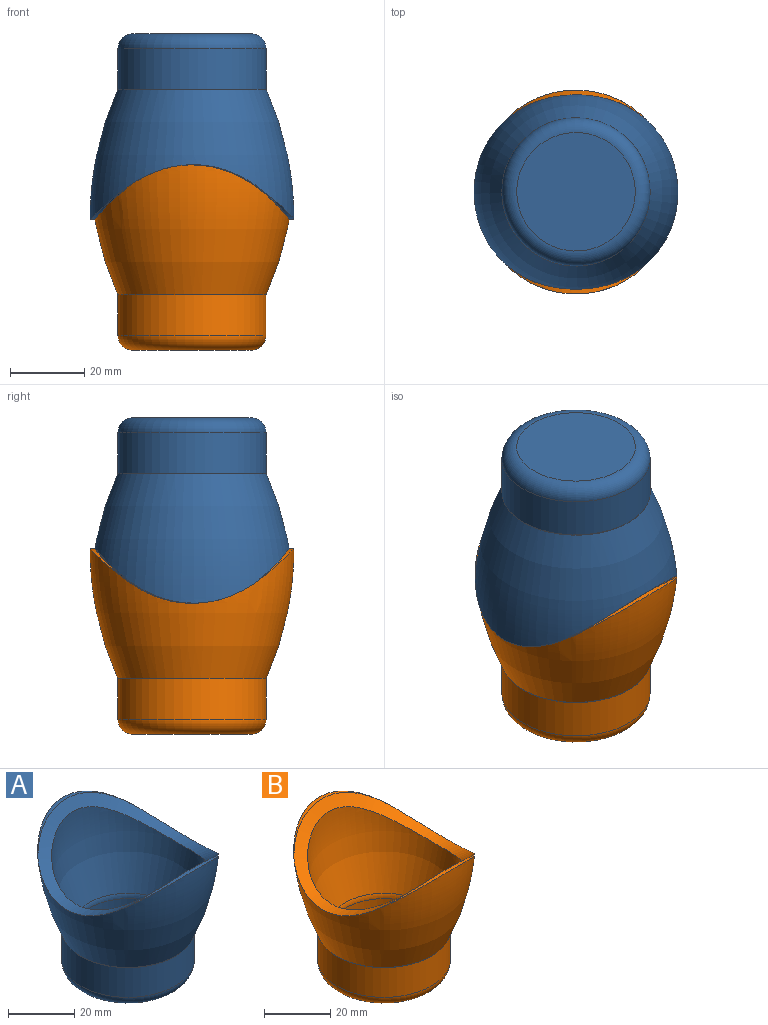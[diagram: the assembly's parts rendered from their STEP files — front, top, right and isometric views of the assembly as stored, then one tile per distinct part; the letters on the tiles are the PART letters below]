
ASSEMBLY  parts=2 mates=1
PART A: 12 faces, bbox 54.9x55x50 mm
  f0: revolved ~54.94x54.94mm, area 4386.3mm2, adj f1,f2,f6,f7
  f1: extruded ~40.09x9.24mm, area 34.4mm2, adj f0,f7
  f2: extruded ~40.09x9.24mm, area 34.3mm2, adj f0,f7
  f3: plane 32x32mm, normal (0,0,-1), area 804.2mm2, adj f5
  f4: cylinder r=20mm len=40mm, axis (0,0,-1), area 1376.9mm2, adj f5,f6
  f5: torus R=16mm, axis (0,0,-1), area 732.2mm2, adj f3,f4
  f6: torus R=20.2mm, axis (0,0,-1), area 10.6mm2, adj f0,f4
  f7: extruded ~52.46x52.45mm, area 724.9mm2, adj f0,f1,f2,f11
  f8: plane 32x32mm, normal (0,0,1), area 804.2mm2, adj f9
  f9: cylinder r=16mm len=32mm, axis (0,0,-1), area 1101.5mm2, adj f8,f10
  f10: torus R=20.2mm, axis (0,0,-1), area 179.4mm2, adj f9,f11
  f11: revolved ~46.86x46.86mm, area 3196.2mm2, adj f7,f10
PART B: 12 faces, bbox 54.9x55x50 mm
  f0: revolved ~54.94x54.94mm, area 4386.3mm2, adj f1,f2,f6,f7
  f1: extruded ~40.09x9.24mm, area 34.4mm2, adj f0,f7
  f2: extruded ~40.09x9.24mm, area 34.3mm2, adj f0,f7
  f3: plane 32x32mm, normal (0,0,-1), area 804.2mm2, adj f5
  f4: cylinder r=20mm len=40mm, axis (0,0,-1), area 1376.9mm2, adj f5,f6
  f5: torus R=16mm, axis (0,0,-1), area 732.2mm2, adj f3,f4
  f6: torus R=20.2mm, axis (0,0,-1), area 10.6mm2, adj f0,f4
  f7: extruded ~52.46x52.45mm, area 724.9mm2, adj f0,f1,f2,f11
  f8: plane 32x32mm, normal (0,0,1), area 804.2mm2, adj f9
  f9: cylinder r=16mm len=32mm, axis (0,0,-1), area 1101.5mm2, adj f8,f10
  f10: torus R=20.2mm, axis (0,0,-1), area 179.4mm2, adj f9,f11
  f11: revolved ~46.86x46.86mm, area 3196.2mm2, adj f7,f10
PLACE A rot(axis=(0.71,-0.7,0),180deg) t=(0.43,0.15,109.31)mm
PLACE B t=(0.43,0.15,-26.06)mm fixed
MATE cylindrical A.f4 <-> B.f4  axis (0,0,1) through (0.43,0.15,55.31)mm
